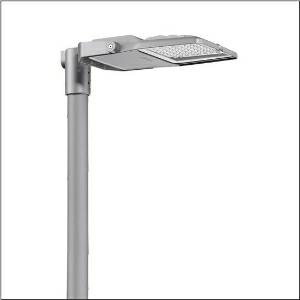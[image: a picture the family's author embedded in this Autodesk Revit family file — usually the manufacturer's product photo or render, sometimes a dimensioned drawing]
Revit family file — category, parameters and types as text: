
# Revit family: floodlight_fl_21_mini___pl64_5xa7772d4e3a_a383
name_source: partatom
category: Lighting Fixtures
units: mm (PartAtom-declared; Revit-internal decimal feet)

## family parameters
Cut with Voids When Loaded = No
Host = Face
Light Source = No
Part Type = Normal
Room Calculation Point = No
Round Connector Dimension = Use Diameter
Shared = No

## types (1)
- --- (1 x LED, 17970 lm, 143 W, 4000K)
    Apparent Load = 143 VA
    CIE Flux Codes = 28 80 98 100 100
    Color Rendering = 70
    Color Temperature = 4000K
    Default Elevation = 1800 mm
    Description = Floodlight FL 21 mini, floodlight, primary light control with lens, of PMMA, primary optical cover: protective disc, of toughened safety glass, transparent, light distribution: PL64, light emission: direct distribution, installation type: surface-mounted, LED, High Power LED, rated luminous flux: 17.970lm, luminous efficacy: 126lm/W, light colour: 740, colour temperature: 4000K, control gear: ECG iQ, control: Auto-Match, Temp-Guard, Night-Set, Smart-Wire, Desk-Remote (wireless, voltage-free reading and setting of iQ features in the workshop via application-optimized NFC function/RFID function), optimised constant luminous flux control (CLO 2.0), Light-Fading, Lumen-Switch, with terminal, 6-pole, mains connection: 220..240V, AC, 50/60Hz, start of lifetime: 143W, end of lifetime: 152W, reduction: 61W, luminaire housing, of diecast aluminium, powder-coated, Siteco® metallic grey (DB 702S), corrosivity category C5 according to DIN EN ISO 12944, mast bracket, of steel, galvanised, powder-coated, protection rating (complete): IP66, insulation class (complete): insulation class II (safety insulation), certification: CE, ENEC, VDE, protection symbol: D, impact resistance: IK08, permissible operating ambient temperature: -40..+40°C, permissible operating ambient temperature for outdoor applications: -40..+50°C, standard: DIN EN 12944, packaging unit: 1 piece

Light Distribution: PL64
    Height = 70 mm
    Lamp = 1 x LED
    Lamp Light Flux = 17970 lm
    Lamp Power = 143 W
    Lamp count = 1
    Length = 485 mm
    Luminous efficacy = 126 lm/W
    Manufacturer = Siteco
    ModVariant = No
    Model = 5XA7772D4E3A
    Number of Poles = 1
    OnlyDefault = Yes
    Power Factor = 1
    Product Name = Floodlight FL 21 mini | PL64
    Product group = floodlight | pylon top
    ProductGroupID = 6101
    Protection Class = Protection class II
    Protection Degree = IP 66
    RLX_Detail_Level = 1
    RlxData = <blob elided: 101353 chars, md5=fba3c1c4>
    Socket = socket
    Standby Power = 0 W
    System Light Flux = 17970 lm
    System Power = 143 W
    Type Comments = factory setting: luminous flux: 100 % | dim-lin: 254 | 730 mA
    Type Image = l_1007125.jpg
    URL = http://relux.com
    VarID = @adj_076701
    Voltage = 0 V
    Weight = 0.00 kg
    Width = 337 mm

## geometry (parser evidence)
native form markers: Blend x4, Sweep x12
no freeform markers — native parametric forms only
